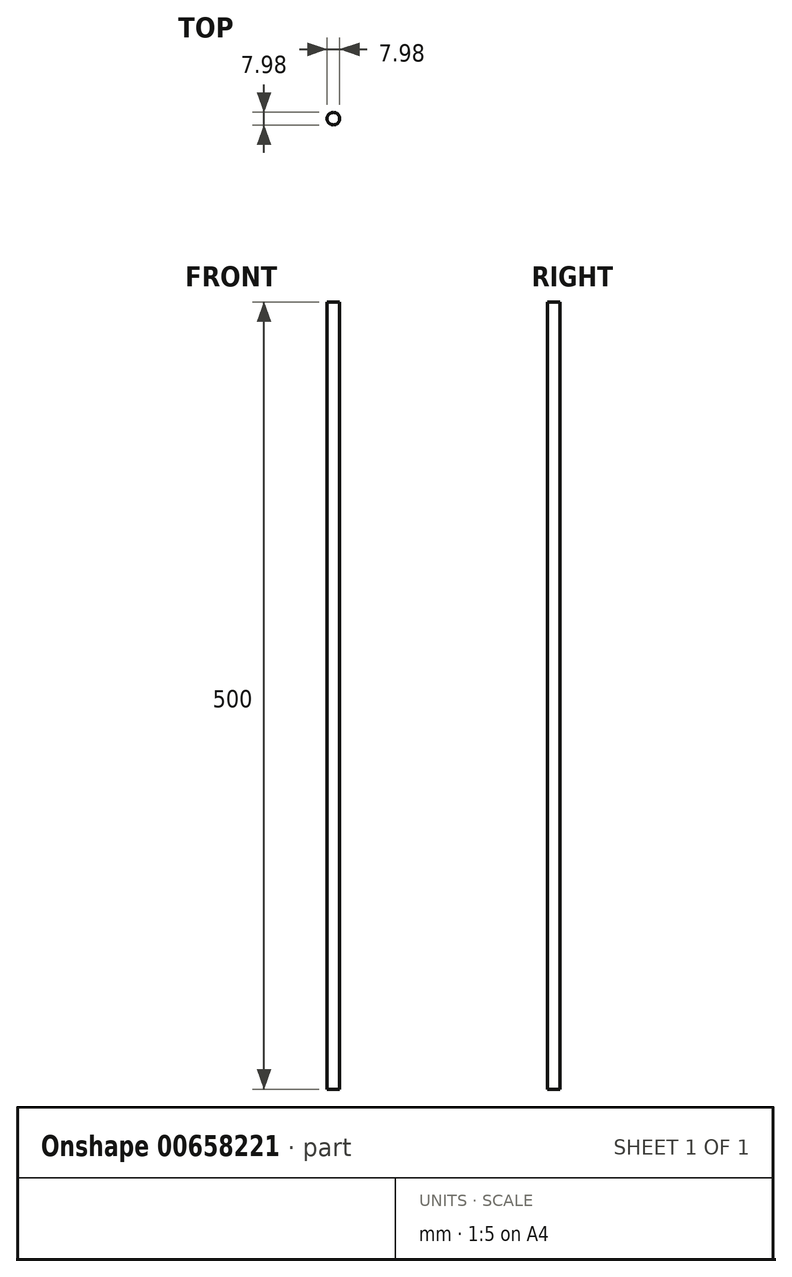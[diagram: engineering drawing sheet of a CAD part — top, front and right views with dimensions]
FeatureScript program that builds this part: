
annotation { "Feature Type Name" : "Feature", "Feature Type Description" : "" }
export const myFeature = defineFeature(function(context is Context, id is Id, definition is map)
    precondition{}
    {
        {
            var Q0;
            Q0=qCreatedBy(makeId("Top.planeOp"),FACE);
            var sketch = newSketch(context, id + "F0", { "sketchPlane" : qUnion([Q0])});
            skCircle(sketch, "E0", {"center": v(0, 0) * mm, "radius": 3.99 * mm});
            skSolve(sketch);
        }
        {
            var Q0;
            Q0=makeQuery(id+"F0.imprint","IMPRINT",FACE,{"disambiguationData":[TD([[makeQuery(id+"F0.imprint","IMPRINT",EDGE,{"derivedFrom":sQuery(id+"F0.wireOp",EDGE,"E0")}),1.0]])]});
            extrude(context, id + "F1", {"entities" : qUnion([Q0]), "depth" : 500 * mm, "offsetDistance" : 25.4 * mm});
        }
    });
